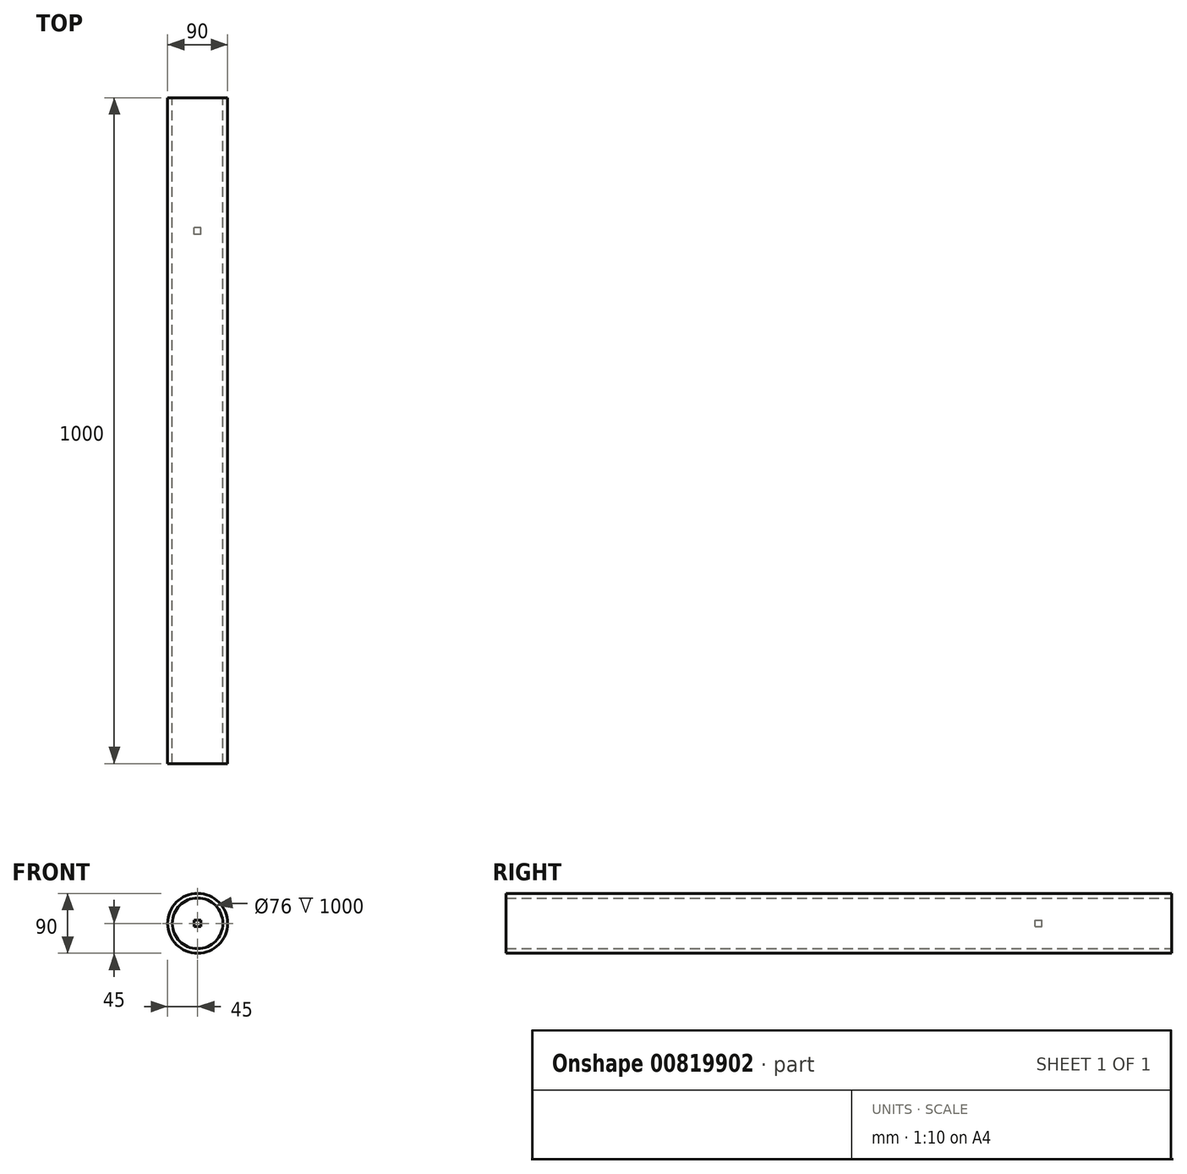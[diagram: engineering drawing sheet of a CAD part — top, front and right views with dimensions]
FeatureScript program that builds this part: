
annotation { "Feature Type Name" : "Feature", "Feature Type Description" : "" }
export const myFeature = defineFeature(function(context is Context, id is Id, definition is map)
    precondition{}
    {
        {
            var Q0;
            Q0=qCreatedBy(makeId("Front.planeOp"),FACE);
            var sketch = newSketch(context, id + "F0", { "sketchPlane" : qUnion([Q0])});
            skCircle(sketch, "E0", {"center": v(0, 0) * mm, "radius": 45 * mm});
            skCircle(sketch, "E1", {"center": v(0, 0) * mm, "radius": 38 * mm});
            skSolve(sketch);
        }
        {
            var Q0;
            Q0=qSketchRegion(id+"F0",true);
            extrude(context, id + "F1", {"entities" : qUnion([Q0]), "depth" : 1000 * mm, "offsetDistance" : 25 * mm});
        }
        {
            var Q0;
            Q0=qCreatedBy(makeId("Right.planeOp"),FACE);
            var sketch = newSketch(context, id + "F2", { "sketchPlane" : qUnion([Q0])});
            skLineSegment(sketch, "E2", {"start": v(0, 0) * mm, "end": v(-200, 0) * mm});
            skLineSegment(sketch, "E3.bottom", {"start": v(-205, -5) * mm, "end": v(-195, -5) * mm});
            skLineSegment(sketch, "E3.top", {"start": v(-205, 5) * mm, "end": v(-195, 5) * mm});
            skLineSegment(sketch, "E3.left", {"start": v(-205, -5) * mm, "end": v(-205, 5) * mm});
            skLineSegment(sketch, "E3.right", {"start": v(-195, -5) * mm, "end": v(-195, 5) * mm});
            skPoint(sketch, "E3.middle", {"position": v(-200, 0) * mm});
            skSolve(sketch);
        }
        {
            var Q0;
            Q0=qSketchRegion(id+"F2",true);
            extrude(context, id + "F3", {"entities" : qUnion([Q0]), "endBound" : BoundingType.SYMMETRIC, "depth" : 10 * mm, "offsetDistance" : 25 * mm});
        }
    });
